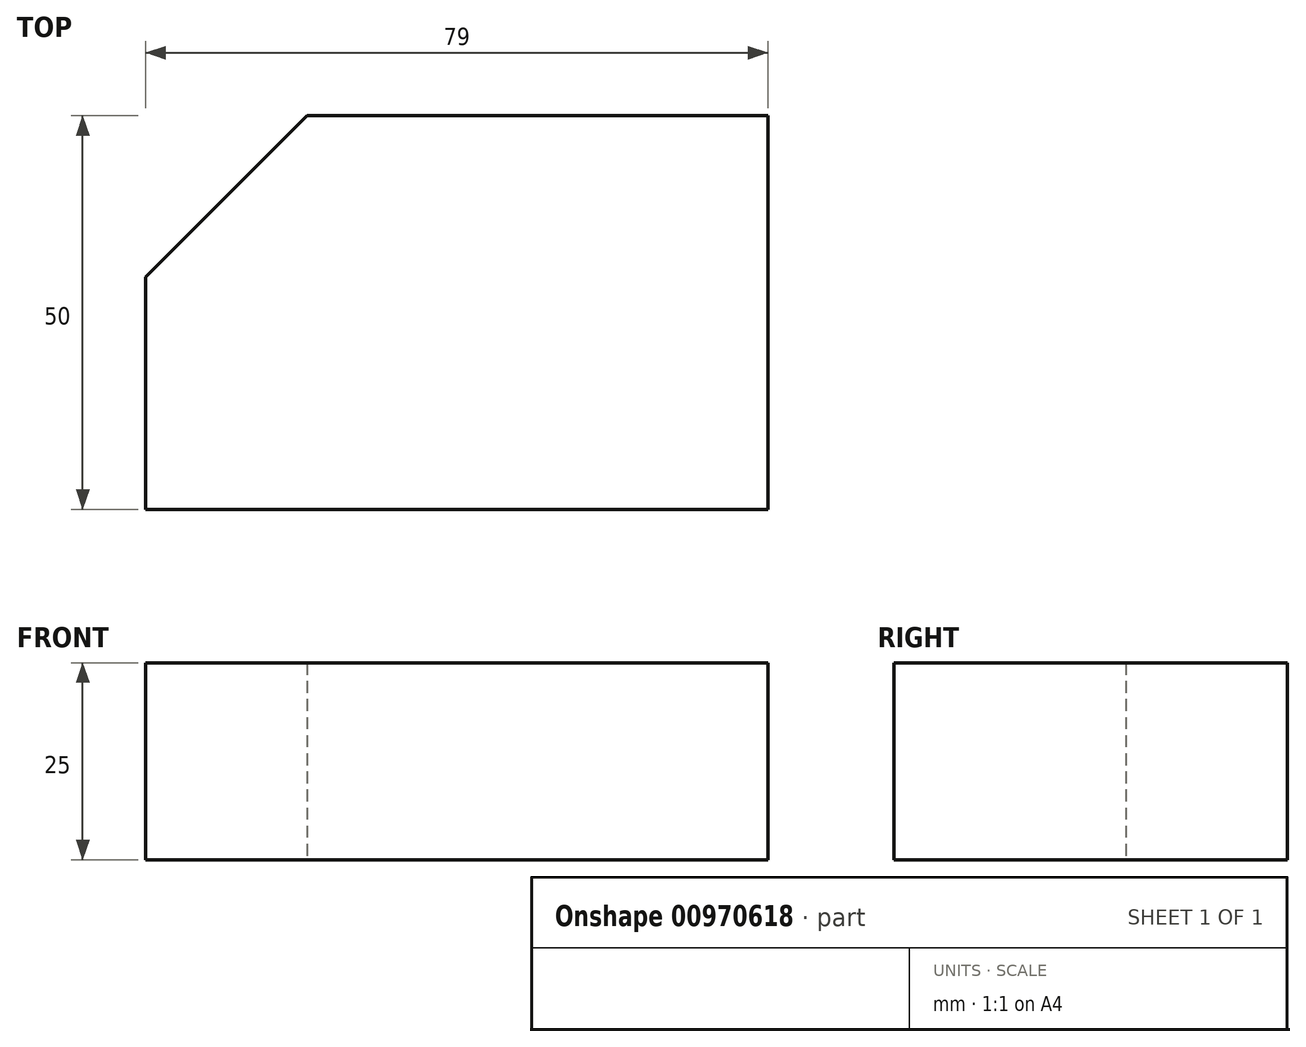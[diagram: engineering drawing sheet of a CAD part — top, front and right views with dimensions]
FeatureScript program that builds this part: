
annotation { "Feature Type Name" : "Feature", "Feature Type Description" : "" }
export const myFeature = defineFeature(function(context is Context, id is Id, definition is map)
    precondition{}
    {
        {
            var Q0;
            Q0=qCreatedBy(makeId("Top.planeOp"),FACE);
            var sketch = newSketch(context, id + "F0", { "sketchPlane" : qUnion([Q0])});
            skLineSegment(sketch, "E0", {"start": v(0, 25) * mm, "end": v(0, -25) * mm, "construction": true});
            skLineSegment(sketch, "E1", {"start": v(-39.5, 0) * mm, "end": v(39.5, 0) * mm, "construction": true});
            skLineSegment(sketch, "E2.bottom", {"start": v(-39.5, 25) * mm, "end": v(39.5, 25) * mm});
            skLineSegment(sketch, "E2.top", {"start": v(-39.5, -25) * mm, "end": v(39.5, -25) * mm});
            skLineSegment(sketch, "E2.left", {"start": v(-39.5, 25) * mm, "end": v(-39.5, -25) * mm});
            skLineSegment(sketch, "E2.right", {"start": v(39.5, 25) * mm, "end": v(39.5, -25) * mm});
            skLineSegment(sketch, "E3", {"start": v(-39.5, 4.5) * mm, "end": v(-19, 25) * mm});
            skSolve(sketch);
        }
        {
            var Q0;
            {var subQ2=sQuery(id+"F0.wireOp",EDGE,"E2.top");Q0=makeQuery(id+"F0.imprint","IMPRINT",FACE,{"disambiguationData":[TD([[makeQuery(id+"F0.imprint","IMPRINT",EDGE,{"derivedFrom":subQ2}),1.0]])]});}
            extrude(context, id + "F1", {"entities" : qUnion([Q0]), "depth" : 25 * mm, "offsetDistance" : 25 * mm});
        }
    });
